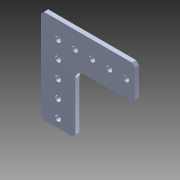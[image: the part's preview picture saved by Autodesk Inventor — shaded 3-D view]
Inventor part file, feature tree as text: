
AUTODESK INVENTOR PART (.ipt)
format: ipt  version: 2014 (Build 180170000, 170)  size: 160,256 bytes
history: native  units: in
note: dims shown in document units (in); Inventor stores cm internally (conversion verified against a paired STEP export)
features: other x2, extrude x1, imported_body x1, sketch x1
ambient origin geometry x8: Origin, YZ Plane, XZ Plane, XY Plane, X Axis, Y Axis, Z Axis, Center Point
bodies: Body1 (feature_tree)
feature tree (5):
  other  "Break-Corner1"
  other  "217-3548-STEP1"
  extrude  "Extrusion1"  [1 undecoded]
  imported_body  "Base1"
  sketch  "Sketch1"  dims[d0=0.035in d1=0.0in]
note: 1 required parameter value undecoded (feature->parameter linkage not recoverable at this tier; creation-order binding heuristic only, values carry confidence <= 0.55)
